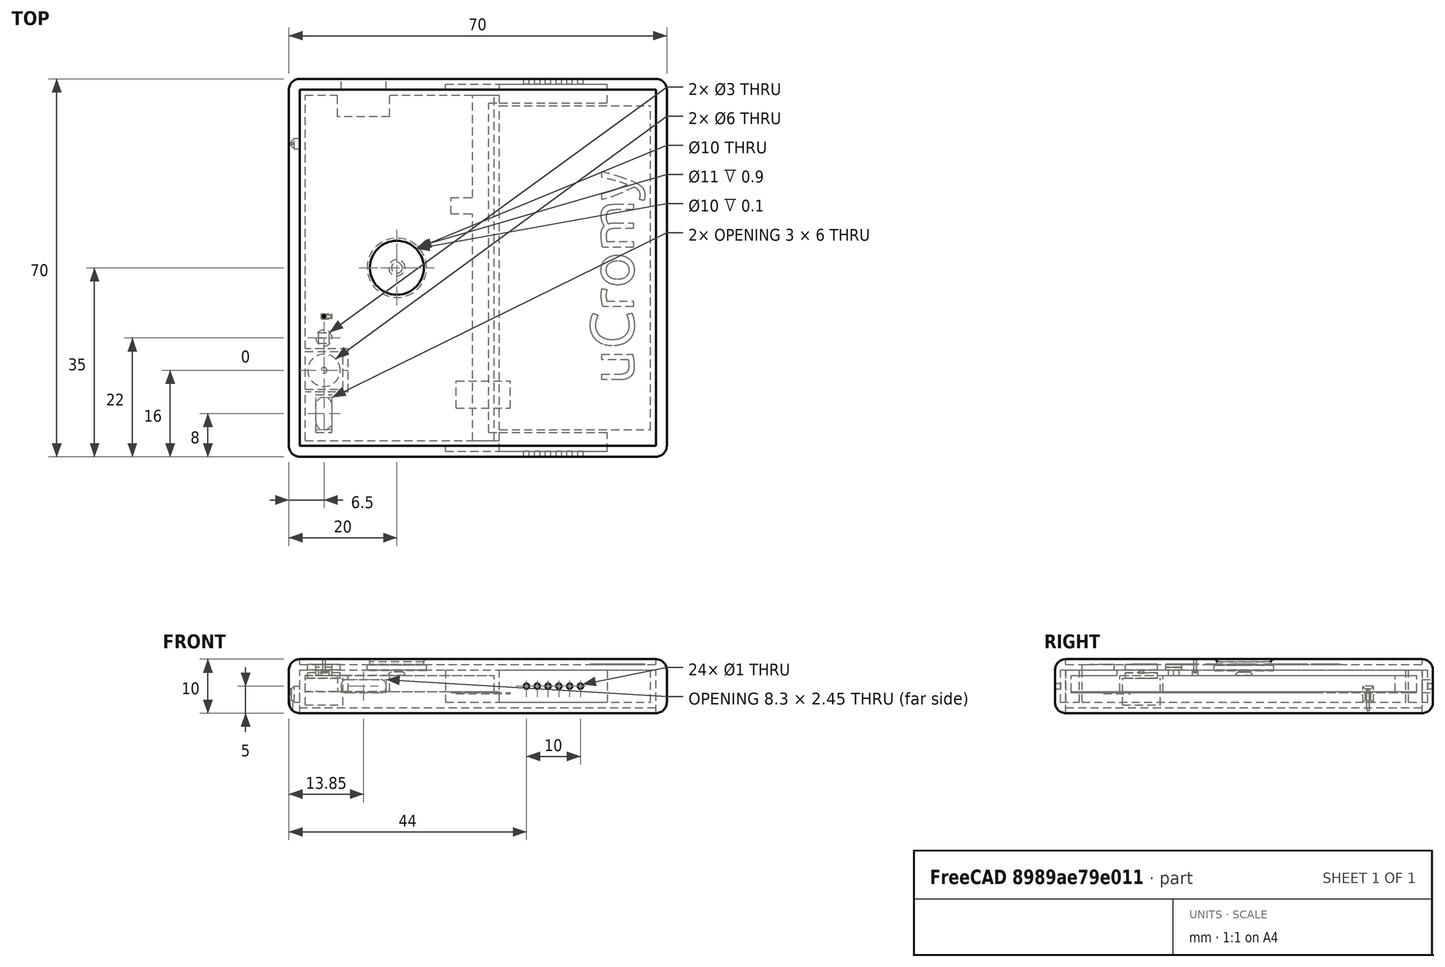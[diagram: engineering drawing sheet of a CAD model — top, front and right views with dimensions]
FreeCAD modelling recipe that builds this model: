
FCSTD DOCUMENT  (FreeCAD 0.16R6706 (Git))
Label: uCromy 2017 for blinds
License: All rights reserved
LicenseURL: http://en.wikipedia.org/wiki/All_rights_reserved
objects: Part::Cylinder×29, Part::Box×28, Part::Cut×27, Part::Feature×16, Part::Extrusion×14, Part::MultiFuse×7, Part::Fillet×6, Part::Chamfer×2
note: 129 computed .brp shape members not serialized (recipe doc carries the construction recipe); baked Part::Feature solids carry a one-line shape summary decoded from their .brp

FEATURE [Part::Box] Box  label="Cubo"
  Height = 10
  Length = 70
  Width = 70
FEATURE [Part::Fillet] Fillet
  Base = -> Box
  Edges = 12 edges r=2: [Edge1,Edge2,Edge3,Edge4,Edge5,Edge6,Edge7,Edge8,Edge9,Edge10,Edge11,Edge12]
FEATURE [Part::Box] Box001  label="Cubo001"
  Height = 10
  Length = 66
  Placement = pos=(2,2,-2) rot=(0,0,1;0rad)
  Width = 66
FEATURE [Part::Box] Box002  label="Tapa"
  Height = 1
  Length = 66
  Placement = pos=(2,2,0) rot=(0,0,1;0rad)
  Width = 66
FEATURE [Part::Box] Box003  label="Cubo003"
  Height = 13
  Length = 3
  Placement = pos=(5,5,0) rot=(0,0,1;0rad)
  Width = 6
FEATURE [Part::Fillet] Fillet001
  Base = -> Box003
  Edges = 4 edges r=1.49: [Edge1,Edge3,Edge5,Edge7]
FEATURE [Part::Box] Box004  label="Cubo004"
  Height = 3
  Length = 66
  Placement = pos=(2,2,9) rot=(0,0,1;0rad)
  Width = 66
FEATURE [Part::Box] Box005  label="Cubo005"
  Height = 1
  Length = 66
  Placement = pos=(2,2,9) rot=(0,0,1;0rad)
  Width = 66
FEATURE [Part::Box] Box006  label="Battery"
  Height = 6
  Length = 28
  Placement = pos=(39,5,2) rot=(0,0,1;0rad)
  Width = 60
FEATURE [Part::Box] Box007  label="Cubo007"
  Height = 3
  Length = 35
  Placement = pos=(3,3,4) rot=(0,0,1;0rad)
  Width = 64
FEATURE [Part::Cut] Cut
  Base = -> Fillet
  Tool = -> Box001
FEATURE [Part::Cut] Cut001
  Base = -> Cut
  Tool = -> Fillet001
FEATURE [Part::Cut] Cut002
  Base = -> Cut001
  Tool = -> Box004
FEATURE [Part::Cylinder] Cylinder  label="Cilindro"
  Angle = 360
  Height = 10
  Placement = pos=(6.5,16,0) rot=(0,0,1;0rad)
  Radius = 3
FEATURE [Part::Cut] Cut003
  Base = -> Cut002
  Tool = -> Cylinder
FEATURE [Part::Cylinder] Cylinder001  label="Cilindro001"
  Angle = 360
  Height = 10
  Placement = pos=(6.5,22,0) rot=(0,0,1;0rad)
  Radius = 1.5
FEATURE [Part::Cut] Cut004
  Base = -> Cut003
  Tool = -> Cylinder001
FEATURE [Part::Box] Box008  label="Cubo008"
  Height = 5
  Length = 7
  Placement = pos=(3,12.5,1) rot=(0,0,1;0rad)
  Width = 7
FEATURE [Part::Cylinder] Cylinder002  label="Cilindro002"
  Angle = 360
  Height = 1
  Placement = pos=(6.5,16,6) rot=(0,0,1;0rad)
  Radius = 3
FEATURE [Part::Cylinder] Cylinder003  label="Cilindro003"
  Angle = 360
  Height = 2
  Placement = pos=(6.5,16,6) rot=(0,0,1;0rad)
  Radius = 0.54
FEATURE [Part::Cylinder] Cylinder004  label="Cilindro004"
  Angle = 360
  Height = 1.4
  Placement = pos=(6.5,16,6) rot=(0,0,1;0rad)
  Radius = 0.54
FEATURE [Part::Cut] Cut005
  Base = -> Cylinder002
  Tool = -> Cylinder003
FEATURE [Part::Fillet] Fillet002
  Base = -> Cylinder004
  Edges = 1 edges r=0.5: [Edge1]
FEATURE [Part::Box] Box009  label="Cubo009"
  Height = 6
  Length = 9
  Placement = pos=(2,12,2) rot=(0,0,1;0rad)
  Width = 8
FEATURE [Part::Cut] Cut006  label="PCB"
  Base = -> Box007
  Tool = -> Box009
FEATURE [Part::MultiFuse] Fusion  label="Cámara"
  Placement = pos=(0,0,0.5) rot=(0,0,1;0rad)
  Shapes = -> [Fillet002,Cut005,Box008]
FEATURE [Part::Box] Box010  label="Cubo010"
  Height = 1
  Length = 3
  Placement = pos=(5,4.5,7) rot=(0,0,1;0rad)
  Width = 7
FEATURE [Part::Box] Box011  label="Cubo011"
  Height = 6
  Length = 20
  Placement = pos=(29,1,2) rot=(0,0,1;0rad)
  Width = 3.5
FEATURE [Part::Box] Box012  label="Cubo012"
  Height = 6
  Length = 20
  Placement = pos=(29,65.5,2) rot=(0,0,1;0rad)
  Width = 3.5
FEATURE [Part::Cut] Cut007
  Base = -> Cut004
  Tool = -> Box012
FEATURE [Part::Box] Box013  label="Altavz R"
  Height = 6
  Length = 20
  Placement = pos=(39,65.5,2) rot=(0,0,1;0rad)
  Width = 3.5
FEATURE [Part::Cut] Cut008
  Base = -> Cut007
  Tool = -> Box011
FEATURE [Part::Box] Box014  label="Altavz L"
  Height = 6
  Length = 20
  Placement = pos=(39,1,2) rot=(0,0,1;0rad)
  Width = 3.5
FEATURE [Part::Cylinder] Cylinder005  label="Cilindro005"
  Angle = 360
  Height = 10
  Placement = pos=(32,-2,5) rot=(-0.57735,-0.57735,-0.57735;2.0944rad)
  Radius = 0.5
FEATURE [Part::Cylinder] Cylinder006  label="Cilindro006"
  Angle = 360
  Height = 10
  Placement = pos=(34,-2,5) rot=(-0.57735,-0.57735,-0.57735;2.0944rad)
  Radius = 0.5
FEATURE [Part::Cylinder] Cylinder007  label="Cilindro007"
  Angle = 360
  Height = 10
  Placement = pos=(36,-2,5) rot=(-0.57735,-0.57735,-0.57735;2.0944rad)
  Radius = 0.5
FEATURE [Part::Cylinder] Cylinder008  label="Cilindro008"
  Angle = 360
  Height = 10
  Placement = pos=(38,-2,5) rot=(-0.57735,-0.57735,-0.57735;2.0944rad)
  Radius = 0.5
FEATURE [Part::Cylinder] Cylinder009  label="Cilindro009"
  Angle = 360
  Height = 10
  Placement = pos=(40,-2,5) rot=(-0.57735,-0.57735,-0.57735;2.0944rad)
  Radius = 0.5
FEATURE [Part::Cylinder] Cylinder010  label="Cilindro010"
  Angle = 360
  Height = 10
  Placement = pos=(42,-2,5) rot=(-0.57735,-0.57735,-0.57735;2.0944rad)
  Radius = 0.5
FEATURE [Part::MultiFuse] Fusion001
  Placement = pos=(12,0,0) rot=(0,0,1;0rad)
  Shapes = -> [Cylinder005,Cylinder006,Cylinder007,Cylinder008,Cylinder009,Cylinder010]
FEATURE [Part::Cylinder] Cylinder011  label="Cilindro011"
  Angle = 360
  Height = 10
  Placement = pos=(32,-2,5) rot=(-0.57735,-0.57735,-0.57735;2.0944rad)
  Radius = 0.5
FEATURE [Part::Cylinder] Cylinder012  label="Cilindro012"
  Angle = 360
  Height = 10
  Placement = pos=(34,-2,5) rot=(-0.57735,-0.57735,-0.57735;2.0944rad)
  Radius = 0.5
FEATURE [Part::Cylinder] Cylinder013  label="Cilindro013"
  Angle = 360
  Height = 10
  Placement = pos=(36,-2,5) rot=(-0.57735,-0.57735,-0.57735;2.0944rad)
  Radius = 0.5
FEATURE [Part::Cylinder] Cylinder014  label="Cilindro014"
  Angle = 360
  Height = 10
  Placement = pos=(38,-2,5) rot=(-0.57735,-0.57735,-0.57735;2.0944rad)
  Radius = 0.5
FEATURE [Part::Cylinder] Cylinder015  label="Cilindro015"
  Angle = 360
  Height = 10
  Placement = pos=(40,-2,5) rot=(-0.57735,-0.57735,-0.57735;2.0944rad)
  Radius = 0.5
FEATURE [Part::Cylinder] Cylinder016  label="Cilindro016"
  Angle = 360
  Height = 10
  Placement = pos=(42,-2,5) rot=(-0.57735,-0.57735,-0.57735;2.0944rad)
  Radius = 0.5
FEATURE [Part::MultiFuse] Fusion002
  Placement = pos=(12,64,0) rot=(0,0,1;0rad)
  Shapes = -> [Cylinder011,Cylinder012,Cylinder013,Cylinder014,Cylinder015,Cylinder016]
FEATURE [Part::Cut] Cut009
  Base = -> Cut008
  Tool = -> Fusion002
FEATURE [Part::Cut] Cut010
  Base = -> Cut009
  Tool = -> Fusion001
FEATURE [Part::Cylinder] Cylinder017  label="Cilindro017"
  Angle = 360
  Height = 10
  Placement = pos=(6.5,26,0) rot=(0,0,1;0rad)
  Radius = 0.25
FEATURE [Part::Cylinder] Cylinder018  label="Cilindro018"
  Angle = 360
  Height = 15
  Placement = pos=(6.5,26,0) rot=(0,0,1;0rad)
  Radius = 0.25
FEATURE [Part::Cut] Cut011
  Base = -> Cut010
  Tool = -> Cylinder017
FEATURE [Part::Cut] Cut012
  Base = -> Box005
  Tool = -> Cylinder018
FEATURE [Part::Box] Box015  label="Cubo015"
  Height = 1
  Length = 2
  Placement = pos=(5.5,21,7) rot=(0,0,1;0rad)
  Width = 1
FEATURE [Part::Box] Box016  label="Cubo016"
  Height = 1
  Length = 2
  Placement = pos=(5.5,22,7) rot=(0,0,1;0rad)
  Width = 1
FEATURE [Part::Cylinder] Cylinder019  label="Lente Flash"
  Angle = 360
  Height = 0.5
  Placement = pos=(6.5,22,8.5) rot=(0,0,1;0rad)
  Radius = 1.5
FEATURE [Part::Box] Box017  label="Altavoz R"
  Height = 6
  Length = 20
  Placement = pos=(39,65.5,2) rot=(0,0,1;0rad)
  Width = 3.5
FEATURE [Part::Cut] Cut013
  Base = -> Cut011
  Tool = -> Box013
FEATURE [Part::Box] Box018  label="Altavoz L"
  Height = 6
  Length = 20
  Placement = pos=(39,1,2) rot=(0,0,1;0rad)
  Width = 3.5
FEATURE [Part::Cut] Cut014
  Base = -> Cut013
  Tool = -> Box014
FEATURE [Part::Cylinder] Cylinder020  label="Cilindro020"
  Angle = 360
  Height = 10
  Placement = pos=(-3,58,4) rot=(0.57735,0.57735,0.57735;2.0944rad)
  Radius = 0.25
FEATURE [Part::Cut] Cut015
  Base = -> Cut014
  Tool = -> Cylinder020
FEATURE [Part::Box] Box019  label="Cubo017"
  Height = 3
  Length = 3
  Placement = pos=(0,53,0) rot=(0,0,1;0rad)
  Width = 2
FEATURE [Part::Chamfer] Chamfer
  Base = -> Box019
  Edges = 4 edges r=0.5: [Edge1,Edge2,Edge3,Edge4]
  Placement = pos=(0.5,4,2) rot=(0,0,1;0rad)
FEATURE [Part::Cut] Cut016
  Base = -> Cut015
  Tool = -> Chamfer
FEATURE [Part::Cylinder] Cylinder021  label="Cilindro021"
  Angle = 360
  Height = 10
  Placement = pos=(0.5,58,-5.5) rot=(0,0,1;0rad)
  Radius = 0.25
FEATURE [Part::Cut] Cut017  label="Don't show"
  Base = -> Cut016
  Tool = -> Cylinder021
FEATURE [Part::Box] Box020  label="Cubo018"
  Height = 1
  Length = 2
  Placement = pos=(6,25.5,7) rot=(0,0,1;0rad)
  Width = 1
FEATURE [Part::Chamfer] Chamfer001
  Base = -> Box020
  Edges = 4 edges r=0.2: [Edge2,Edge6,Edge10,Edge12]
FEATURE [Part::Cylinder] Cylinder022  label="Cilindro022"
  Angle = 360
  Height = 1.5
  Placement = pos=(6.5,26,7.5) rot=(0,0,1;0rad)
  Radius = 0.25
FEATURE [Part::Cut] Cut018
  Base = -> Chamfer001
  Tool = -> Cylinder022
FEATURE [Part::Box] Box021  label="Cubo019"
  Height = 0.2
  Length = 3
  Placement = pos=(34,3,3.8) rot=(0,0,1;0rad)
  Width = 64
FEATURE [Part::Box] Box022  label="Cubo020"
  Height = 0.2
  Length = 3
  Placement = pos=(36,3,3.8) rot=(0,0,1;0rad)
  Width = 1.5
FEATURE [Part::Box] Box023  label="Cubo021"
  Height = 0.2
  Length = 3
  Placement = pos=(36,65.5,3.8) rot=(0,0,1;0rad)
  Width = 1.5
FEATURE [Part::Box] Box024  label="Cubo022"
  Height = 0.2
  Length = 4
  Placement = pos=(30,45,3.8) rot=(0,0,1;0rad)
  Width = 3
FEATURE [Part::MultiFuse] Fusion003  label="Don't show001"
  Shapes = -> [Box021,Box024,Box023,Box022]
FEATURE [Part::Feature] Fusion003001  label="Flex Altavoces"
  shape: bbox 9 x 64 x 0.2 mm, 14 faces (baked)
FEATURE [Part::Feature] Cut017001  label="Cut019"
  shape: bbox 70 x 70 x 10 mm, 79 faces (baked)
FEATURE [Part::Box] Box025  label="Flex Batería"
  Height = 0.2
  Length = 10
  Placement = pos=(31,9,3.6) rot=(0,0,1;0rad)
  Width = 5
FEATURE [Part::Cylinder] Cylinder023  label="Cilindro023"
  Angle = 360
  Height = 10
  Placement = pos=(20,35,0) rot=(0,0,1;0rad)
  Radius = 5
FEATURE [Part::Cut] Cut017002
  Base = -> Cut012
  Tool = -> Cylinder023
FEATURE [Part::Cut] Cut017003
  Base = -> Cut017001
  Tool = -> Cylinder023
FEATURE [Part::Cylinder] Cylinder024  label="Cilindro024"
  Angle = 360
  Height = 0.6
  Placement = pos=(20,35,8.9) rot=(0,0,1;0rad)
  Radius = 5
FEATURE [Part::Fillet] Fillet003  label="Cut017008"
  Base = -> Cut017002
  Edges = 1 edges r=0.5: [Edge10]
FEATURE [Part::Cylinder] Cylinder025  label="Cilindro025"
  Angle = 360
  Height = 2
  Placement = pos=(20,35,6.9) rot=(0,0,1;0rad)
  Radius = 5.5
FEATURE [Part::Cut] Cut017004  label="Chasis"
  Base = -> Cut017003
  Tool = -> Cylinder025
FEATURE [Part::Cylinder] Cylinder026  label="Cilindro026"
  Angle = 360
  Height = 1
  Placement = pos=(20,35,7.9) rot=(0,0,1;0rad)
  Radius = 5.5
FEATURE [Part::Cylinder] Cylinder027  label="Cilindro027"
  Angle = 360
  Height = 0.2
  Placement = pos=(20,35,7.8) rot=(0,0,1;0rad)
  Radius = 1
FEATURE [Part::Cylinder] Cylinder028  label="Cilindro028"
  Angle = 360
  Height = 0.6
  Placement = pos=(20,35,7) rot=(0,0,1;0rad)
  Radius = 1.5
FEATURE [Part::Fillet] Fillet004  label="PowerButton"
  Base = -> Cylinder028
  Edges = 1 edges r=0.5: [Edge1]
FEATURE [Part::MultiFuse] Fusion003002  label="Huella dactilar"
  Shapes = -> [Cylinder027,Cylinder026,Cylinder024]
FEATURE [Part::Feature] path3344
  shape: bbox 4.741 x 5.994 x 2e-07 mm, 0 faces, 0 solids (baked)
FEATURE [Part::Feature] path3346
  shape: bbox 6.062 x 8.173 x 2e-07 mm, 0 faces, 0 solids (baked)
FEATURE [Part::Feature] path3348
  shape: bbox 3.342 x 5.994 x 2e-07 mm, 0 faces, 0 solids (baked)
FEATURE [Part::Feature] path3350
  shape: bbox 5.509 x 6.164 x 2e-07 mm, 0 faces, 0 solids (baked)
FEATURE [Part::Feature] path3350001
  shape: bbox 3.319 x 4.312 x 2e-07 mm, 0 faces, 0 solids (baked)
FEATURE [Part::Feature] path3352
  shape: bbox 7.981 x 5.994 x 2e-07 mm, 0 faces, 0 solids (baked)
FEATURE [Part::Feature] path3354
  shape: bbox 5.385 x 7.993 x 2e-07 mm, 0 faces, 0 solids (baked)
FEATURE [Part::Extrusion] Extrude
  Base = -> path3344
  Dir = (0,0,0.1)
  Solid = true
FEATURE [Part::Extrusion] Extrude001
  Base = -> path3346
  Dir = (0,0,0.1)
  Solid = true
FEATURE [Part::Extrusion] Extrude002
  Base = -> path3348
  Dir = (0,0,0.1)
  Solid = true
FEATURE [Part::Extrusion] Extrude003
  Base = -> path3350
  Dir = (0,0,0.1)
  Solid = true
FEATURE [Part::Extrusion] Extrude004
  Base = -> path3350001
  Dir = (0,0,0.1)
  Solid = true
FEATURE [Part::Extrusion] Extrude005
  Base = -> path3352
  Dir = (0,0,0.1)
  Solid = true
FEATURE [Part::Extrusion] Extrude006
  Base = -> path3354
  Dir = (0,0,0.1)
  Solid = true
FEATURE [Part::Cut] Cut017005
  Base = -> Extrude003
  Tool = -> Extrude004
FEATURE [Part::MultiFuse] Fusion003003  label="uCromy Logo"
  Placement = pos=(5.5,-14,9) rot=(0,0,1;1.5708rad)
  Shapes = -> [Extrude,Extrude006,Extrude005,Cut017005,Extrude001,Extrude002]
FEATURE [Part::Feature] path3350002
  shape: bbox 4.741 x 5.994 x 2e-07 mm, 0 faces, 0 solids (baked)
FEATURE [Part::Feature] path3350003
  shape: bbox 6.062 x 8.173 x 2e-07 mm, 0 faces, 0 solids (baked)
FEATURE [Part::Feature] path3350004
  shape: bbox 3.342 x 5.994 x 2e-07 mm, 0 faces, 0 solids (baked)
FEATURE [Part::Feature] path3350005
  shape: bbox 5.509 x 6.164 x 2e-07 mm, 0 faces, 0 solids (baked)
FEATURE [Part::Feature] path3350006
  shape: bbox 3.319 x 4.312 x 2e-07 mm, 0 faces, 0 solids (baked)
FEATURE [Part::Feature] path3350007
  shape: bbox 7.981 x 5.994 x 2e-07 mm, 0 faces, 0 solids (baked)
FEATURE [Part::Feature] path3350008
  shape: bbox 5.385 x 7.993 x 2e-07 mm, 0 faces, 0 solids (baked)
FEATURE [Part::Extrusion] Extrude007
  Base = -> path3350002
  Dir = (0,0,0.1)
  Solid = true
FEATURE [Part::Extrusion] Extrude008
  Base = -> path3350003
  Dir = (0,0,0.1)
  Solid = true
FEATURE [Part::Extrusion] Extrude009
  Base = -> path3350004
  Dir = (0,0,0.1)
  Solid = true
FEATURE [Part::Extrusion] Extrude010
  Base = -> path3350005
  Dir = (0,0,0.1)
  Solid = true
FEATURE [Part::Extrusion] Extrude011
  Base = -> path3350006
  Dir = (0,0,0.1)
  Solid = true
FEATURE [Part::Extrusion] Extrude012
  Base = -> path3350007
  Dir = (0,0,0.1)
  Solid = true
FEATURE [Part::Extrusion] Extrude013
  Base = -> path3350008
  Dir = (0,0,0.1)
  Solid = true
FEATURE [Part::Cut] Cut017006
  Base = -> Extrude010
  Tool = -> Extrude011
FEATURE [Part::MultiFuse] Fusion003004  label="uCromy Logo001"
  Placement = pos=(5.5,-14,9) rot=(0,0,1;1.5708rad)
  Shapes = -> [Extrude007,Extrude013,Extrude012,Cut017006,Extrude008,Extrude009]
FEATURE [Part::Cut] Cut017007  label="Cristal"
  Base = -> Fillet003
  Tool = -> Fusion003004
FEATURE [Part::Box] Box035  label="Cubo029"
  Height = 2.45
  Length = 8.65
  Width = 8.3
FEATURE [Part::Fillet] Fillet022  label="USB-C003"
  Base = -> Box035
  Edges = 4 edges r=1: [Edge9,Edge10,Edge11,Edge12]
  Placement = pos=(18,64.35,3.775) rot=(0,0,1;1.5708rad)
FEATURE [Part::Box] Box036  label="Cubo030"
  Height = 10
  Length = 9.65
  Placement = pos=(9,63,0) rot=(0,0,1;0rad)
  Width = 10
FEATURE [Part::Cut] Cut017008  label="Cut017009"
  Base = -> Cut006
  Tool = -> Box036
FEATURE [Part::Cut] Cut017009  label="Cut017010"
  Base = -> Cut017004
  Tool = -> Fillet022
